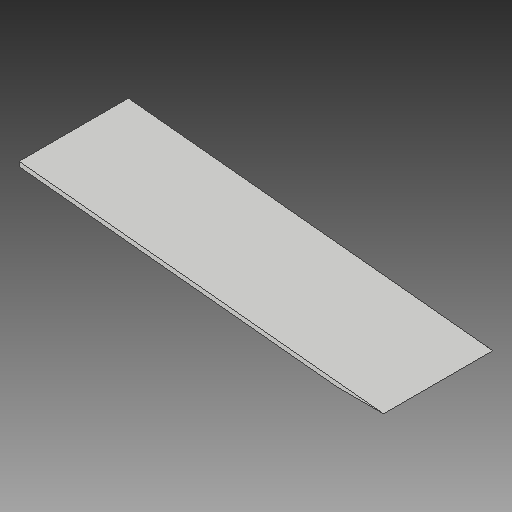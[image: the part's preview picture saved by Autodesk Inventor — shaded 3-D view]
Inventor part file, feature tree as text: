
AUTODESK INVENTOR PART (.ipt)
format: ipt  version: 2019 (Build 230136000, 136)  size: 93,696 bytes
history: native  units: in
note: dims shown in document units (in); Inventor stores cm internally (conversion verified against a paired STEP export)
features: other x5, reference x3, extrude x1, sketch x1
ambient origin geometry x8: Origin, YZ Plane, XZ Plane, XY Plane, X Axis, Y Axis, Z Axis, Center Point
bodies: Solid1 (feature_tree)
feature tree (10):
  extrude  "Extrusion1"  Depth=18.0in
  sketch  "Sketch1"  dims[d3=0.75in d4=78.0in d5=18.0in d6=0.0in]
  reference  "Reference1"
  reference  "Reference2"
  reference  "Reference3"
  other  "<userpath>\Desktop\Roombotics\UpperLevel.iam"
  other  "UpperLevel.iam"
  other  "Top:1"
  other  "Side1:2"
  other  "Side1:1"
